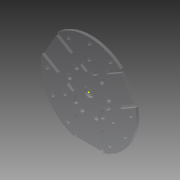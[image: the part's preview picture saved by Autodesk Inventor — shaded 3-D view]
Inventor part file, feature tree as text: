
AUTODESK INVENTOR PART (.ipt)
format: ipt  version: 2015 (Build 190159000, 159)  size: 271,360 bytes
history: native  units: mm
features: sketch x7, extrude x6, projected_geometry x3, pattern_circular x2
ambient origin geometry x8: Origin, YZ Plane, XZ Plane, XY Plane, X Axis, Y Axis, Z Axis, Center Point
bodies: Solid1 (feature_tree)
feature tree (18):
  extrude  "Extrusion1"  Depth=3.0mm TaperAngle=0.0deg
  extrude  "Extrusion2"  Depth=7.0mm
  extrude  "Extrusion3"  Depth=11.724mm
  extrude  "Extrusion4"  Depth=3.0mm
  extrude  "Extrusion5"  Depth=3.0mm TaperAngle=0.0deg
  pattern_circular  "Circular Pattern1"  [2 undecoded]
  sketch  "Sketch6"  dims[d12=5.0mm]
  pattern_circular  "Circular Pattern2"  [2 undecoded]
  extrude  "Extrusion6"  Depth=3.0mm TaperAngle=0.0deg
  sketch  "Sketch1"  dims[d0=103.0mm d1=3.0mm d2=0.0mm]
  sketch  "Sketch2"  dims[d3=10.906mm d4=7.0mm]
  projected_geometry  "Projected Loop1"
  sketch  "Sketch3"  dims[d5=11.724mm d6=40.0mm]
  sketch  "Sketch4"  dims[d7=32.0mm d8=3.0mm]
  projected_geometry  "Projected Loop2"
  sketch  "Sketch5"  dims[d9=3.0mm d10=3.0mm d11=0.0mm]
  sketch  "Sketch7"  dims[d13=15.0mm d14=20.006mm d15=5.0mm d16=3.0mm d17=0.0mm d18=3.0mm d19=0.0mm d20=48.0mm d21=10.0mm d22=3.0mm d23=0.0mm d24=30.0mm d25=360.0deg d27=30.0mm d28=360.0deg d30=60.0mm d31=90.0mm d32=30.0deg d33=30.0deg d34=30.0deg d35=30.0deg d36=30.0deg d37=30.0deg d38=120.0deg d39=120.0deg d40=3.0mm d41=3.0mm d42=3.0mm d43=3.0mm d44=3.0mm d45=3.0mm d46=3.0mm d47=3.0mm d48=3.0mm d49=3.0mm d50=3.0mm d51=3.0mm d52=3.0mm d53=0.0mm]
  projected_geometry  "Projected Loop3"
note: 4 required parameter values undecoded (feature->parameter linkage not recoverable at this tier; creation-order binding heuristic only, values carry confidence <= 0.55)
